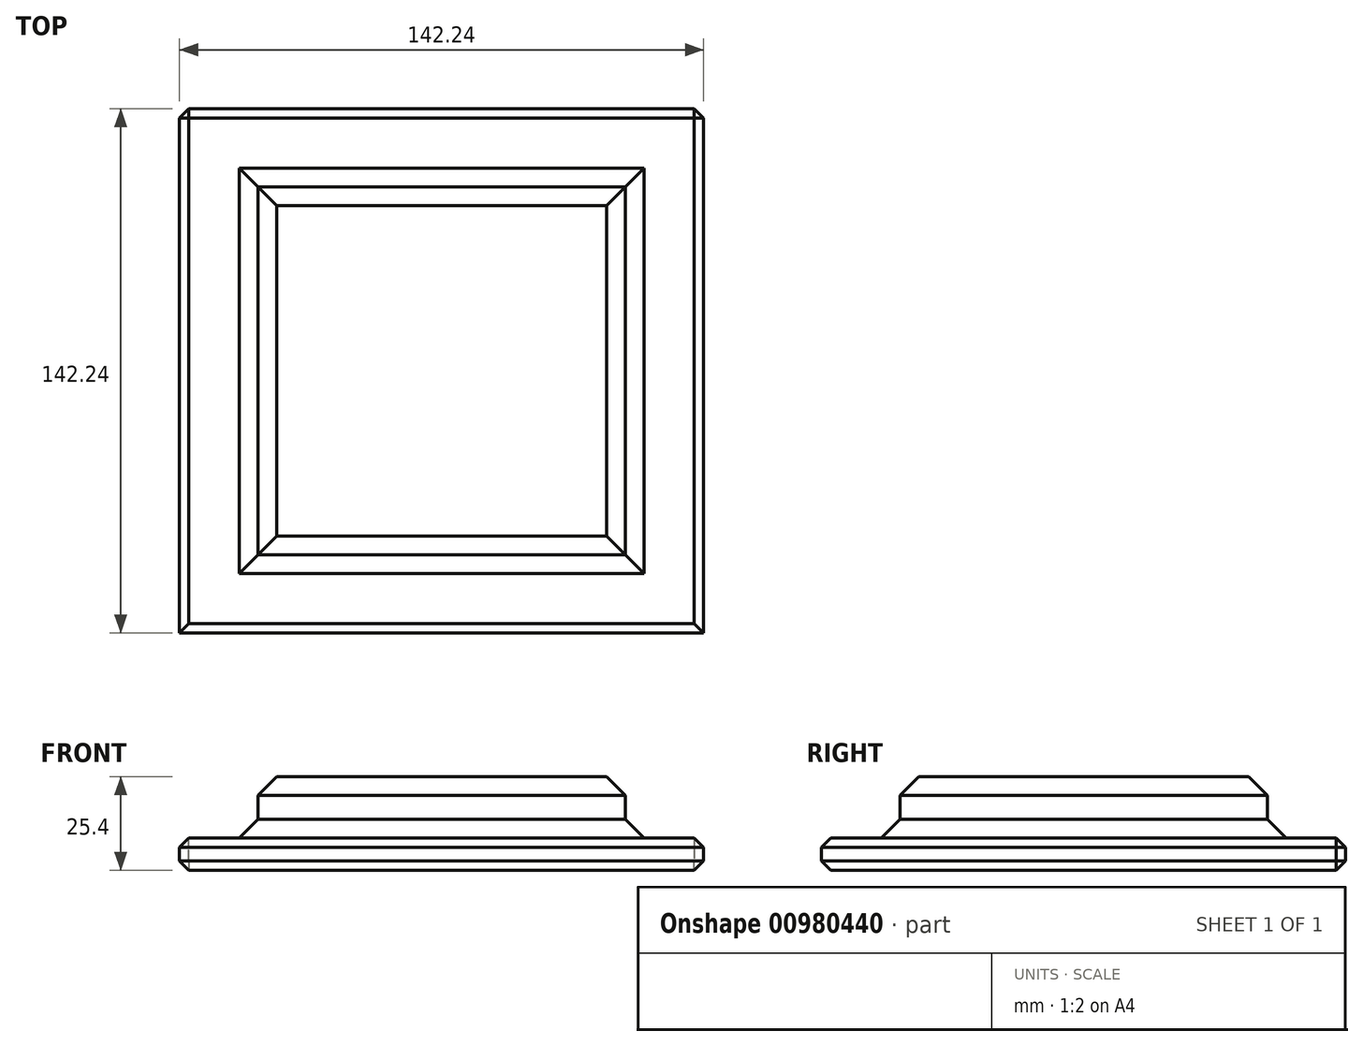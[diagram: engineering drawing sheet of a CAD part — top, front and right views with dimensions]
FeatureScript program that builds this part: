
annotation { "Feature Type Name" : "Feature", "Feature Type Description" : "" }
export const myFeature = defineFeature(function(context is Context, id is Id, definition is map)
    precondition{}
    {
        {
            var Q0;
            Q0=qCreatedBy(makeId("Top.planeOp"),FACE);
            var sketch = newSketch(context, id + "F0", { "sketchPlane" : qUnion([Q0])});
            skLineSegment(sketch, "E0.bottom", {"start": v(-71.12, -71.12) * mm, "end": v(71.12, -71.12) * mm});
            skLineSegment(sketch, "E0.top", {"start": v(-71.12, 71.12) * mm, "end": v(71.12, 71.12) * mm});
            skLineSegment(sketch, "E0.left", {"start": v(-71.12, -71.12) * mm, "end": v(-71.12, 71.12) * mm});
            skLineSegment(sketch, "E0.right", {"start": v(71.12, -71.12) * mm, "end": v(71.12, 71.12) * mm});
            skLineSegment(sketch, "E1", {"start": v(0, 0) * mm, "end": v(0, 71.12) * mm, "construction": true});
            skLineSegment(sketch, "E2", {"start": v(0, 0) * mm, "end": v(71.12, 0) * mm, "construction": true});
            skSolve(sketch);
        }
        {
            var Q0;
            Q0=makeQuery(id+"F0.imprint","IMPRINT",FACE,{"disambiguationData":[TD([[makeQuery(id+"F0.imprint","IMPRINT",EDGE,{"derivedFrom":sQuery(id+"F0.wireOp",EDGE,"E0.bottom")}),1.0]])]});
            extrude(context, id + "F1", {"entities" : qUnion([Q0]), "depth" : 8.76 * mm, "offsetDistance" : 25.4 * mm});
        }
        {
            var Q0;
            Q0=qCreatedBy(makeId("Top.planeOp"),FACE);
            var sketch = newSketch(context, id + "F2", { "sketchPlane" : qUnion([Q0])});
            skLineSegment(sketch, "E3.bottom", {"start": v(49.86, 49.86) * mm, "end": v(-49.86, 49.86) * mm});
            skLineSegment(sketch, "E3.top", {"start": v(49.86, -49.86) * mm, "end": v(-49.86, -49.86) * mm});
            skLineSegment(sketch, "E3.left", {"start": v(49.86, 49.86) * mm, "end": v(49.86, -49.86) * mm});
            skLineSegment(sketch, "E3.right", {"start": v(-49.86, 49.86) * mm, "end": v(-49.86, -49.86) * mm});
            skPoint(sketch, "E3.middle", {"position": v(0, 0) * mm});
            skSolve(sketch);
        }
        {
            var Q0;
            Q0=makeQuery(id+"F2.imprint","IMPRINT",FACE,{"disambiguationData":[TD([[makeQuery(id+"F2.imprint","IMPRINT",EDGE,{"derivedFrom":sQuery(id+"F2.wireOp",EDGE,"E3.bottom")}),1.0]])]});
            extrude(context, id + "F3", {"entities" : qUnion([Q0]), "operationType" : NewBodyOperationType.ADD, "depth" : 25.4 * mm, "offsetDistance" : 25.4 * mm});
        }
        {
            var Q0;
            Q0=makeQuery(id+"F1.opExtrude","SWEPT_FACE",FACE,{"disambiguationData":[OSD([sQuery(id+"F0.wireOp",EDGE,"E0.top")])]});
            var Q1;
            Q1=makeQuery(id+"F1.opExtrude","CAP_EDGE",EDGE,{"disambiguationData":[OSD([sQuery(id+"F0.wireOp",EDGE,"E0.right")])],"isStart":false});
            var Q2;
            Q2=makeQuery(id+"F1.opExtrude","CAP_EDGE",EDGE,{"disambiguationData":[OSD([sQuery(id+"F0.wireOp",EDGE,"E0.right")])],"isStart":true});
            var Q3;
            Q3=makeQuery(id+"F1.opExtrude","CAP_EDGE",EDGE,{"disambiguationData":[OSD([sQuery(id+"F0.wireOp",EDGE,"E0.bottom")])],"isStart":false});
            var Q4;
            Q4=makeQuery(id+"F1.opExtrude","CAP_EDGE",EDGE,{"disambiguationData":[OSD([sQuery(id+"F0.wireOp",EDGE,"E0.bottom")])],"isStart":true});
            var Q5;
            Q5=makeQuery(id+"F1.opExtrude","CAP_EDGE",EDGE,{"disambiguationData":[OSD([sQuery(id+"F0.wireOp",EDGE,"E0.left")])],"isStart":false});
            var Q6;
            Q6=makeQuery(id+"F1.opExtrude","CAP_EDGE",EDGE,{"disambiguationData":[OSD([sQuery(id+"F0.wireOp",EDGE,"E0.left")])],"isStart":true});
            chamfer(context, id + "F4", {"entities" : qUnion([Q0, Q1, Q2, Q3, Q4, Q5, Q6]), "width" : 2.54 * mm, "tangentPropagation" : true});
        }
        {
            var Q0;
            Q0=makeQuery(id+"F3.opExtrude","CAP_EDGE",EDGE,{"disambiguationData":[OSD([sQuery(id+"F2.wireOp",EDGE,"E3.right")])],"isStart":false});
            var Q1;
            Q1=makeQuery(id+"F3.opExtrude","CAP_EDGE",EDGE,{"disambiguationData":[OSD([sQuery(id+"F2.wireOp",EDGE,"E3.bottom")])],"isStart":false});
            var Q2;
            Q2=makeQuery(id+"F3.opExtrude","CAP_FACE",FACE,{"disambiguationData":[OSD([sQuery(id+"F2.wireOp",EDGE,"E3.bottom"),sQuery(id+"F2.wireOp",EDGE,"E3.top"),sQuery(id+"F2.wireOp",EDGE,"E3.left"),sQuery(id+"F2.wireOp",EDGE,"E3.right")])],"isStart":false});
            var Q3;
            Q3=makeQuery(id+"F1.opExtrude","CAP_EDGE",EDGE,{"disambiguationData":[OSD([sQuery(id+"F0.wireOp",EDGE,"E0.left")])],"isStart":false});
            var Q4;
            Q4=makeQuery(id+"F1.opExtrude","CAP_EDGE",EDGE,{"disambiguationData":[OSD([sQuery(id+"F0.wireOp",EDGE,"E0.top")])],"isStart":false});
            var Q5;
            Q5=makeQuery(id+"F1.opExtrude","CAP_EDGE",EDGE,{"disambiguationData":[OSD([sQuery(id+"F0.wireOp",EDGE,"E0.right")])],"isStart":false});
            var Q6;
            Q6=makeQuery(id+"F1.opExtrude","CAP_EDGE",EDGE,{"disambiguationData":[OSD([sQuery(id+"F0.wireOp",EDGE,"E0.bottom")])],"isStart":false});
            var Q7;
            Q7=makeQuery(id+"F3.boolean.opBoolean","INTERSECT",EDGE,{"derivedFrom":[makeQuery(id+"F1.opExtrude","CAP_FACE",FACE,{"disambiguationData":[OSD([sQuery(id+"F0.wireOp",EDGE,"E0.bottom"),sQuery(id+"F0.wireOp",EDGE,"E0.top"),sQuery(id+"F0.wireOp",EDGE,"E0.left"),sQuery(id+"F0.wireOp",EDGE,"E0.right")])],"isStart":false}),makeQuery(id+"F3.opExtrude","SWEPT_FACE",FACE,{"disambiguationData":[OSD([sQuery(id+"F2.wireOp",EDGE,"E3.right")])]})]});
            var Q8;
            Q8=makeQuery(id+"F3.boolean.opBoolean","INTERSECT",EDGE,{"derivedFrom":[makeQuery(id+"F1.opExtrude","CAP_FACE",FACE,{"disambiguationData":[OSD([sQuery(id+"F0.wireOp",EDGE,"E0.bottom"),sQuery(id+"F0.wireOp",EDGE,"E0.top"),sQuery(id+"F0.wireOp",EDGE,"E0.left"),sQuery(id+"F0.wireOp",EDGE,"E0.right")])],"isStart":false}),makeQuery(id+"F3.opExtrude","SWEPT_FACE",FACE,{"disambiguationData":[OSD([sQuery(id+"F2.wireOp",EDGE,"E3.bottom")])]})]});
            var Q9;
            Q9=makeQuery(id+"F3.boolean.opBoolean","INTERSECT",EDGE,{"derivedFrom":[makeQuery(id+"F1.opExtrude","CAP_FACE",FACE,{"disambiguationData":[OSD([sQuery(id+"F0.wireOp",EDGE,"E0.bottom"),sQuery(id+"F0.wireOp",EDGE,"E0.top"),sQuery(id+"F0.wireOp",EDGE,"E0.left"),sQuery(id+"F0.wireOp",EDGE,"E0.right")])],"isStart":false}),makeQuery(id+"F3.opExtrude","SWEPT_FACE",FACE,{"disambiguationData":[OSD([sQuery(id+"F2.wireOp",EDGE,"E3.left")])]})]});
            var Q10;
            Q10=makeQuery(id+"F3.boolean.opBoolean","INTERSECT",EDGE,{"derivedFrom":[makeQuery(id+"F1.opExtrude","CAP_FACE",FACE,{"disambiguationData":[OSD([sQuery(id+"F0.wireOp",EDGE,"E0.bottom"),sQuery(id+"F0.wireOp",EDGE,"E0.top"),sQuery(id+"F0.wireOp",EDGE,"E0.left"),sQuery(id+"F0.wireOp",EDGE,"E0.right")])],"isStart":false}),makeQuery(id+"F3.opExtrude","SWEPT_FACE",FACE,{"disambiguationData":[OSD([sQuery(id+"F2.wireOp",EDGE,"E3.top")])]})]});
            var Q11;
            Q11=makeQuery(id+"F1.opExtrude","CAP_EDGE",EDGE,{"disambiguationData":[OSD([sQuery(id+"F0.wireOp",EDGE,"E0.left")])],"isStart":true});
            var Q12;
            Q12=makeQuery(id+"F1.opExtrude","CAP_EDGE",EDGE,{"disambiguationData":[OSD([sQuery(id+"F0.wireOp",EDGE,"E0.top")])],"isStart":true});
            chamfer(context, id + "F5", {"entities" : qUnion([Q0, Q1, Q2, Q3, Q4, Q5, Q6, Q7, Q8, Q9, Q10, Q11, Q12]), "width" : 5.08 * mm, "tangentPropagation" : true});
        }
    });
